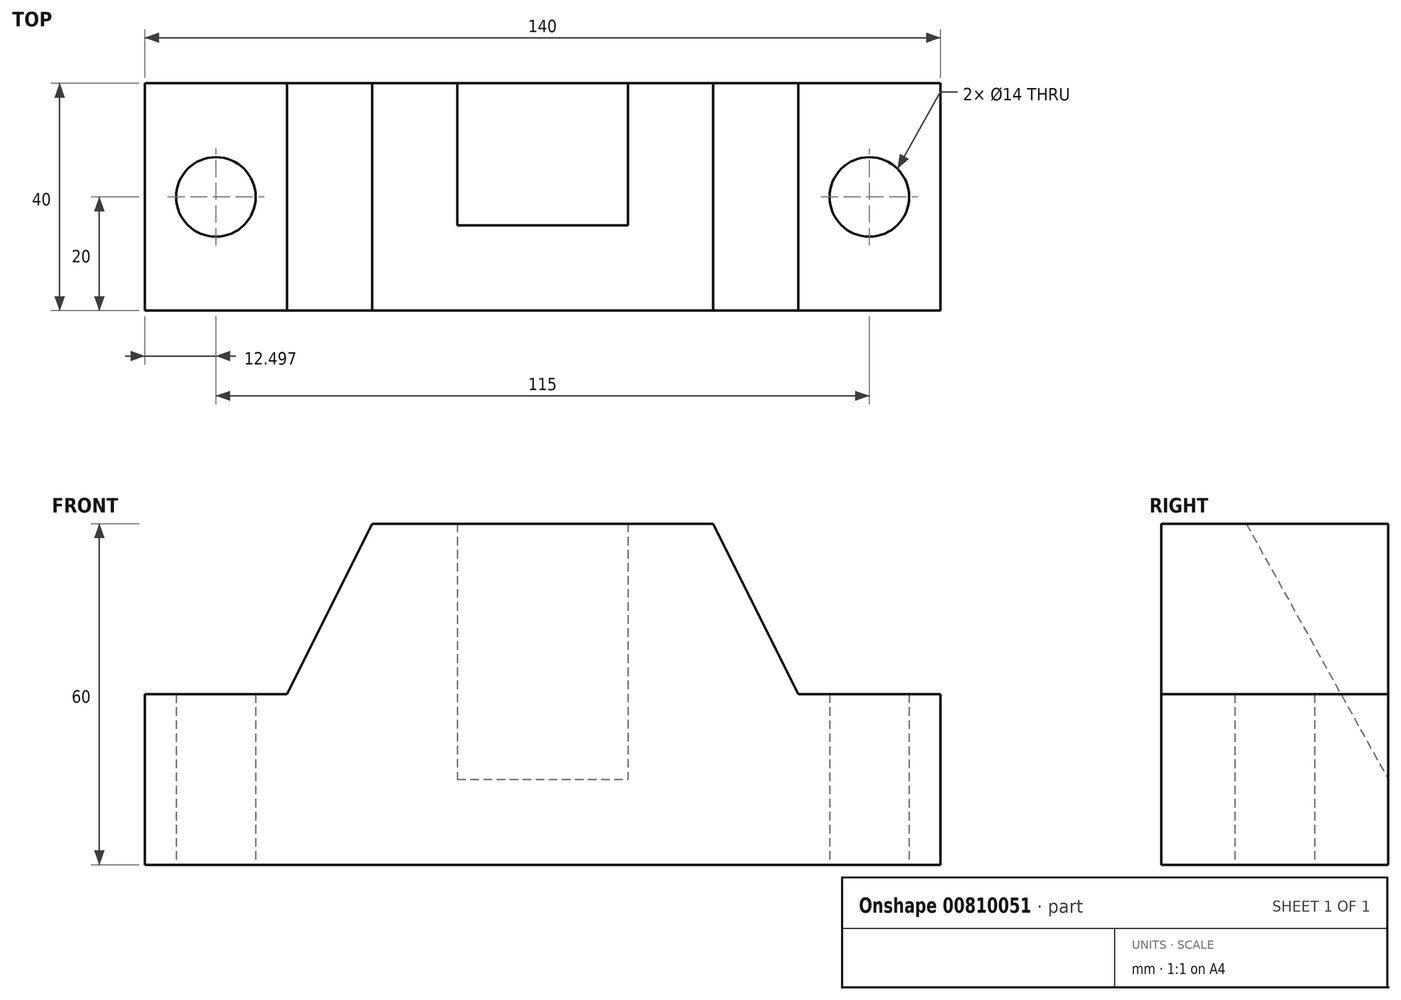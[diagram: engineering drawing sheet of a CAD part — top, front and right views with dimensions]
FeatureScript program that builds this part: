
annotation { "Feature Type Name" : "Feature", "Feature Type Description" : "" }
export const myFeature = defineFeature(function(context is Context, id is Id, definition is map)
    precondition{}
    {
        {
            var Q0;
            Q0=qCreatedBy(makeId("Front.planeOp"),FACE);
            var sketch = newSketch(context, id + "F0", { "sketchPlane" : qUnion([Q0])});
            skLineSegment(sketch, "E0.bottom", {"start": v(-94.3, 42.94) * mm, "end": v(45.7, 42.94) * mm});
            skLineSegment(sketch, "E0.top", {"start": v(-94.3, -17.06) * mm, "end": v(45.7, -17.06) * mm});
            skLineSegment(sketch, "E0.left", {"start": v(-94.3, 42.94) * mm, "end": v(-94.3, -17.06) * mm});
            skLineSegment(sketch, "E0.right", {"start": v(45.7, 42.94) * mm, "end": v(45.7, -17.06) * mm});
            skLineSegment(sketch, "E1", {"start": v(-69.3, 12.94) * mm, "end": v(-69.3, 12.94) * mm});
            skLineSegment(sketch, "E2", {"start": v(-69.3, 12.94) * mm, "end": v(-69.3, 42.94) * mm});
            skLineSegment(sketch, "E3", {"start": v(20.7, 42.94) * mm, "end": v(20.7, 12.94) * mm});
            skLineSegment(sketch, "E4", {"start": v(20.7, 12.94) * mm, "end": v(45.7, 12.94) * mm});
            skLineSegment(sketch, "E5", {"start": v(-69.3, 12.94) * mm, "end": v(-94.3, 12.94) * mm});
            skSolve(sketch);
        }
        {
            var Q0;
            {var subQ1=sQuery(id+"F0.wireOp",EDGE,"E0.top");Q0=makeQuery(id+"F0.imprint","IMPRINT",FACE,{"disambiguationData":[TD([[makeQuery(id+"F0.imprint","IMPRINT",EDGE,{"derivedFrom":subQ1}),1.0]])]});}
            extrude(context, id + "F1", {"entities" : qUnion([Q0]), "depth" : 40 * mm, "offsetDistance" : 25 * mm});
        }
        {
            var Q0;
            Q0=makeQuery(id+"F1.opExtrude","SWEPT_EDGE",EDGE,{"disambiguationData":[OSD([sQuery(id+"F0.wireOp",EDGE,"E0.bottom"),sQuery(id+"F0.wireOp",EDGE,"E2")])]});
            var Q1;
            Q1=makeQuery(id+"F1.opExtrude","SWEPT_EDGE",EDGE,{"disambiguationData":[OSD([sQuery(id+"F0.wireOp",EDGE,"E0.bottom"),sQuery(id+"F0.wireOp",EDGE,"E3")])]});
            chamfer(context, id + "F2", {"entities" : qUnion([Q0, Q1]), "chamferType" : ChamferType.TWO_OFFSETS, "width1" : 30 * mm, "oppositeDirection" : false, "width2" : 15 * mm, "tangentPropagation" : true});
        }
        {
            var Q0;
            Q0=qCreatedBy(makeId("Front.planeOp"),FACE);
            var sketch = newSketch(context, id + "F3", { "sketchPlane" : qUnion([Q0])});
            skLineSegment(sketch, "E6.bottom", {"start": v(-39.3, 42.94) * mm, "end": v(-9.3, 42.94) * mm});
            skLineSegment(sketch, "E6.top", {"start": v(-39.3, -2.06) * mm, "end": v(-9.3, -2.06) * mm});
            skLineSegment(sketch, "E6.left", {"start": v(-39.3, 42.94) * mm, "end": v(-39.3, -2.06) * mm});
            skLineSegment(sketch, "E6.right", {"start": v(-9.3, 42.94) * mm, "end": v(-9.3, -2.06) * mm});
            skSolve(sketch);
        }
        {
            var Q0;
            Q0 = qSketchRegion(id + "F3", true);
            extrude(context, id + "F4", {"entities" : qUnion([Q0]), "operationType" : NewBodyOperationType.REMOVE, "depth" : 25 * mm, "offsetDistance" : 25 * mm});
        }
        {
            var Q0;
            Q0=makeQuery(id+"F4.boolean.opBoolean","COPY",EDGE,{"derivedFrom":makeQuery(id+"F4.opExtrude","CAP_EDGE",EDGE,{"disambiguationData":[OSD([sQuery(id+"F3.wireOp",EDGE,"E6.top")])],"isStart":false})});
            chamfer(context, id + "F5", {"entities" : qUnion([Q0]), "chamferType" : ChamferType.TWO_OFFSETS, "width1" : 25 * mm, "oppositeDirection" : false, "width2" : 45 * mm, "tangentPropagation" : true});
        }
        {
            var Q0;
            Q0=qCreatedBy(makeId("Top.planeOp"),FACE);
            var sketch = newSketch(context, id + "F6", { "sketchPlane" : qUnion([Q0])});
            skCircle(sketch, "E7", {"center": v(-81.8, -20) * mm, "radius": 7 * mm});
            skCircle(sketch, "E8", {"center": v(33.2, -20) * mm, "radius": 7 * mm});
            skSolve(sketch);
        }
        {
            var Q0;
            Q0 = qSketchRegion(id + "F6", true);
            extrude(context, id + "F7", {"entities" : qUnion([Q0]), "operationType" : NewBodyOperationType.REMOVE, "depth" : 15 * mm, "offsetDistance" : 25 * mm, "hasSecondDirection" : true, "secondDirectionOppositeDirection" : true, "secondDirectionDepth" : 20 * mm});
        }
    });
